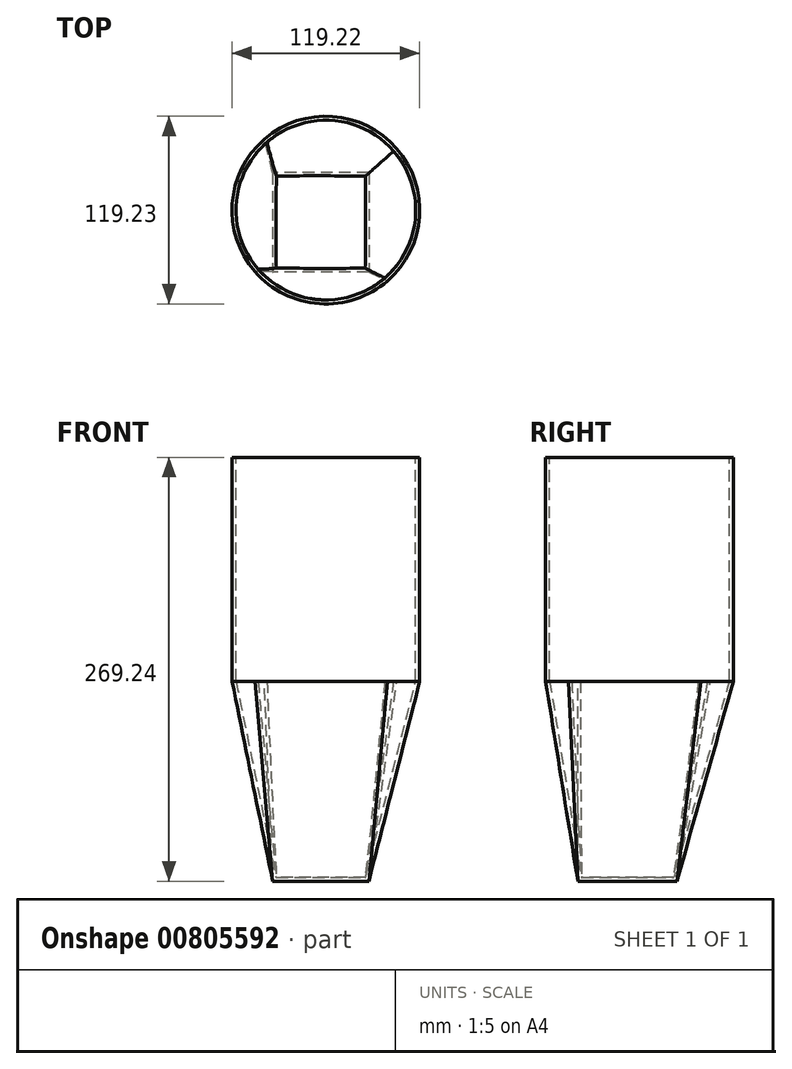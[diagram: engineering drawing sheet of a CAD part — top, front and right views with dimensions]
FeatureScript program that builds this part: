
annotation { "Feature Type Name" : "Feature", "Feature Type Description" : "" }
export const myFeature = defineFeature(function(context is Context, id is Id, definition is map)
    precondition{}
    {
        {
            var Q0;
            Q0=qCreatedBy(makeId("Top.planeOp"),FACE);
            var sketch = newSketch(context, id + "F0", { "sketchPlane" : qUnion([Q0])});
            skLineSegment(sketch, "E0.bottom", {"start": v(30.51, 31.46) * mm, "end": v(-30.51, 31.46) * mm});
            skLineSegment(sketch, "E0.top", {"start": v(30.51, -31.46) * mm, "end": v(-30.51, -31.46) * mm});
            skLineSegment(sketch, "E0.left", {"start": v(30.51, 31.46) * mm, "end": v(30.51, -31.46) * mm});
            skLineSegment(sketch, "E0.right", {"start": v(-30.51, 31.46) * mm, "end": v(-30.51, -31.46) * mm});
            skPoint(sketch, "E0.middle", {"position": v(0, 0) * mm});
            skSolve(sketch);
        }
        {
            var Q0;
            Q0=qCreatedBy(makeId("Top.planeOp"),FACE);
            cPlane(context, id + "F1", {"entities" : qUnion([Q0]), "cplaneType" : CPlaneType.OFFSET, "offset" : 127 * mm, "width" : 152.4 * mm, "height" : 152.4 * mm});
        }
        {
            var Q0;
            Q0=qCreatedBy(id+"F1.planeOp",FACE);
            var sketch = newSketch(context, id + "F2", { "sketchPlane" : qUnion([Q0])});
            skCircle(sketch, "E1", {"center": v(3.25, 7.77) * mm, "radius": 59.61 * mm});
            skSolve(sketch);
        }
        {
            var Q0;
            Q0=makeQuery(id+"F0.imprint","IMPRINT",FACE,{"disambiguationData":[TD([[makeQuery(id+"F0.imprint","IMPRINT",EDGE,{"derivedFrom":sQuery(id+"F0.wireOp",EDGE,"E0.bottom")}),1.0]])]});
            var Q1;
            Q1=makeQuery(id+"F2.imprint","IMPRINT",FACE,{"disambiguationData":[TD([[makeQuery(id+"F2.imprint","IMPRINT",EDGE,{"derivedFrom":sQuery(id+"F2.wireOp",EDGE,"E1")}),1.0]])]});
            loft(context, id + "F3", {"sheetProfilesArray" : [{ "sheetProfileEntities" : qUnion([Q0]) }, { "sheetProfileEntities" : qUnion([Q1]) }]});
        }
        {
            var Q0;
            Q0=makeQuery(id+"F3.opLoft","CAP_FACE",FACE,{"disambiguationData":[OSD([makeQuery(id+"F2.imprint","IMPRINT",FACE,{"disambiguationData":[TD([[makeQuery(id+"F2.imprint","IMPRINT",EDGE,{"derivedFrom":sQuery(id+"F2.wireOp",EDGE,"E1")}),1.0]])]})])],"isStart":true});
            extrude(context, id + "F4", {"entities" : qUnion([Q0]), "operationType" : NewBodyOperationType.ADD, "depth" : 142.24 * mm, "offsetDistance" : 25.4 * mm});
        }
        {
            var Q0;
            Q0=makeQuery(id+"F4.opExtrude","CAP_FACE",FACE,{"disambiguationData":[OSD([makeQuery(id+"F2.imprint","IMPRINT",FACE,{"disambiguationData":[TD([[makeQuery(id+"F2.imprint","IMPRINT",EDGE,{"derivedFrom":sQuery(id+"F2.wireOp",EDGE,"E1")}),1.0]])]})])],"isStart":false});
            shell(context, id + "F5", {"entities" : qUnion([Q0]), "thickness" : 2.54 * mm});
        }
    });
